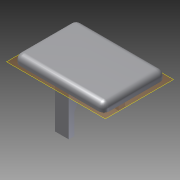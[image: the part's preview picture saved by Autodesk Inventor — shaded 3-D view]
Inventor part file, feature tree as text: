
AUTODESK INVENTOR PART (.ipt)
format: ipt  version: 2012 (Build 160160000, 160)  size: 352,256 bytes
history: native  units: mm
features: extrude x14, sketch x14, projected_geometry x9, reference x4, plane x3, fillet x1
ambient origin geometry x8: Origin, YZ Plane, XZ Plane, XY Plane, X Axis, Y Axis, Z Axis, Center Point
bodies: Solid1 (feature_tree)
feature tree (45):
  extrude  "Extrusion1"  Depth=3.0mm TaperAngle=0.0deg
  plane  "Work Plane1"
  extrude  "Extrusion2"  Depth=0.3mm
  fillet  "Fillet1"  [1 undecoded]
  extrude  "Extrusion3"  Depth=0.3mm
  extrude  "Extrusion4"  Depth=0.3mm
  extrude  "Extrusion5"  TaperAngle=0.0deg  [1 undecoded]
  extrude  "Extrusion6"  Depth=0.3mm
  extrude  "Extrusion7"  Depth=0.3mm
  extrude  "Extrusion8"  Depth=3.0mm TaperAngle=0.0deg
  extrude  "Extrusion9"  Depth=1.5mm
  extrude  "Extrusion10"  Depth=0.891267mm
  extrude  "Extrusion11"  Depth=0.891267mm
  sketch  "Sketch13"  dims[d27=10.0mm d28=0.0mm d29=10.0mm d30=0.0mm]
  plane  "Work Plane2"
  extrude  "Extrusion12"  Depth=10.0mm TaperAngle=0.0deg
  extrude  "Extrusion13"  Depth=1.909188mm
  plane  "Work Plane3"
  extrude  "Extrusion14"  TaperAngle=0.0deg  [1 undecoded]
  sketch  "Sketch1"  dims[d0=14.9mm d1=0.0mm d2=3.0mm d3=0.0mm]
  reference  "Reference1"
  sketch  "Sketch2"  dims[d4=2.0mm d5=0.3mm d6=0.0mm]
  reference  "Reference2"
  projected_geometry  "Projected Loop1"
  projected_geometry  "Projected Loop2"
  sketch  "Sketch3"  dims[d7=0.3mm d8=0.3mm]
  reference  "Reference3"
  sketch  "Sketch4"  dims[d9=0.3mm d10=0.3mm]
  reference  "Reference4"
  projected_geometry  "Projected Loop3"
  projected_geometry  "Projected Loop4"
  sketch  "Sketch6"  dims[d11=0.3mm d12=0.0mm]
  projected_geometry  "Projected Loop5"
  sketch  "Sketch7"  dims[d13=0.3mm d14=0.3mm]
  projected_geometry  "Projected Loop6"
  projected_geometry  "Projected Loop7"
  sketch  "Sketch8"  dims[d15=1.5mm d16=0.3mm]
  sketch  "Sketch9"  dims[d17=0.3mm d18=3.0mm d19=0.0mm]
  projected_geometry  "Projected Loop8"
  sketch  "Sketch10"  dims[d20=1.5mm d21=1.5mm]
  projected_geometry  "Projected Loop9"
  sketch  "Sketch11"  dims[d22=10.0mm d23=0.0mm d24=0.891267mm]
  sketch  "Sketch12"  dims[d25=0.891267mm d26=0.891267mm]
  sketch  "Sketch14"  dims[d31=4.909mm d32=1.909188mm]
  sketch  "Sketch15"  dims[d33=1.499906mm d34=0.0mm d35=2.0mm d36=2.0mm d37=10.0mm d38=0.0mm d39=10.0mm d40=0.0mm d41=10.0mm d42=0.0mm d43=0.4mm d44=0.0mm d45=0.4mm d46=0.0mm d47=10.0mm d48=0.0mm d49=10.0mm d50=0.0mm d51=10.0mm d52=0.0mm]
note: 3 required parameter values undecoded (feature->parameter linkage not recoverable at this tier; creation-order binding heuristic only, values carry confidence <= 0.55)
